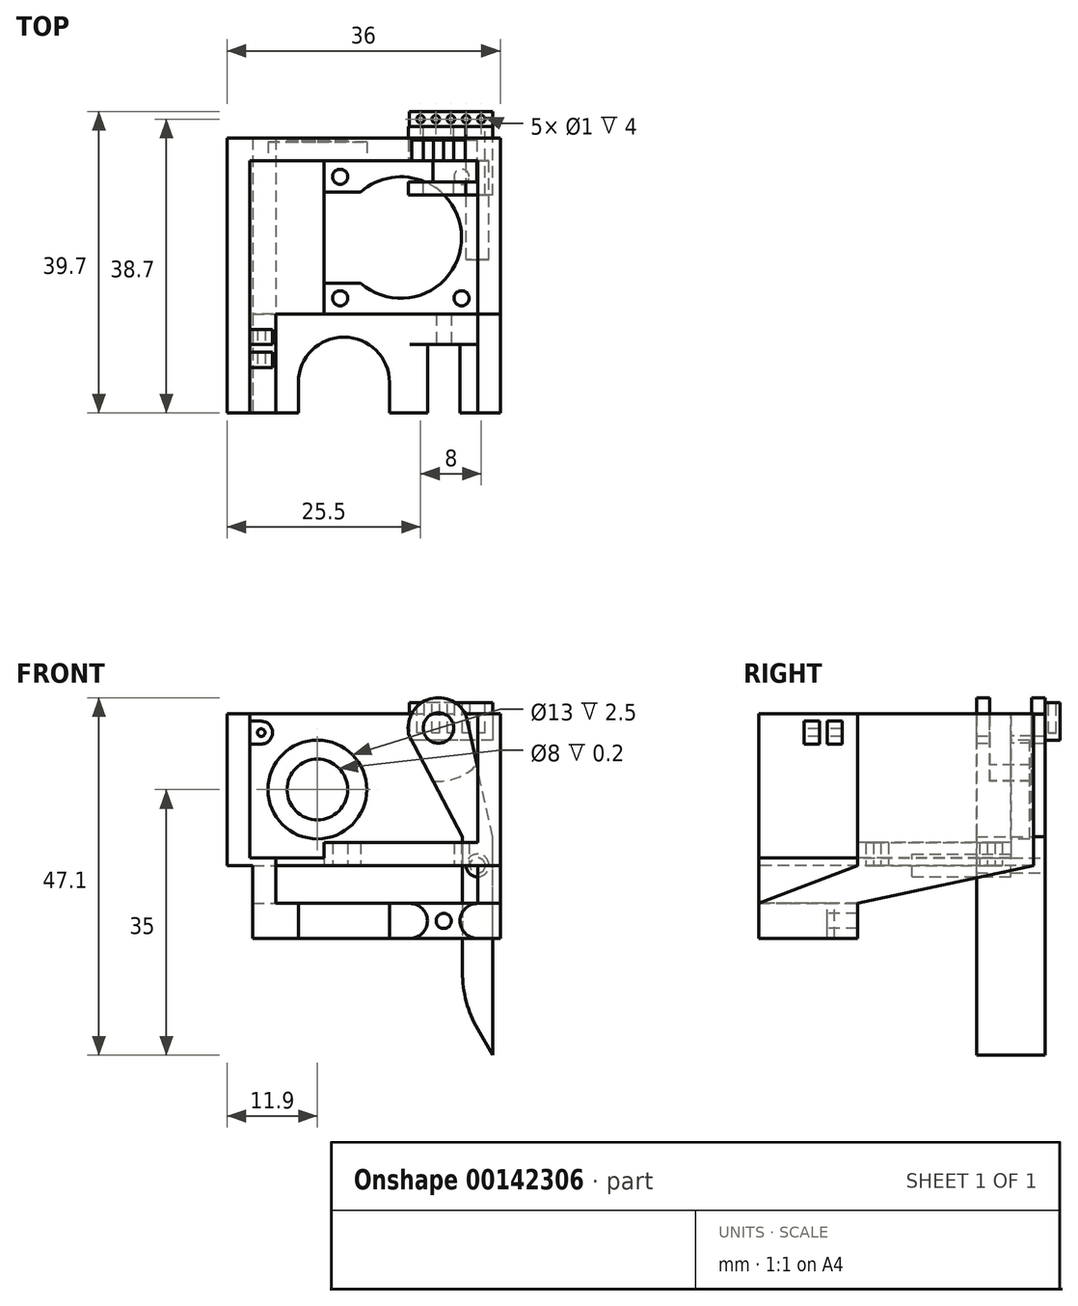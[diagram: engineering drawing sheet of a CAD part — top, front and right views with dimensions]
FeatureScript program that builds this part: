
annotation { "Feature Type Name" : "Feature", "Feature Type Description" : "" }
export const myFeature = defineFeature(function(context is Context, id is Id, definition is map)
    precondition{}
    {
        {
            var Q0;
            Q0=qCreatedBy(makeId("Top.planeOp"),FACE);
            var sketch = newSketch(context, id + "F0", { "sketchPlane" : qUnion([Q0])});
            skLineSegment(sketch, "E0", {"start": v(0, 0) * mm, "end": v(0, -20.2) * mm});
            skLineSegment(sketch, "E1", {"start": v(0, -20.2) * mm, "end": v(3, -20.2) * mm});
            skLineSegment(sketch, "E2", {"start": v(3, -20.2) * mm, "end": v(3, 3) * mm});
            skLineSegment(sketch, "E3", {"start": v(3, 3) * mm, "end": v(-30, 3) * mm});
            skLineSegment(sketch, "E4", {"start": v(-30, 3) * mm, "end": v(-30, 0) * mm});
            skLineSegment(sketch, "E5", {"start": v(-30, 0) * mm, "end": v(0, 0) * mm});
            skLineSegment(sketch, "E6", {"start": v(-4, -20.2) * mm, "end": v(0, -20.2) * mm});
            skCircle(sketch, "E7", {"center": v(-2.1, -2.1) * mm, "radius": 1 * mm});
            skLineSegment(sketch, "E8", {"start": v(3, -20.2) * mm, "end": v(3, -33.2) * mm});
            skLineSegment(sketch, "E9", {"start": v(3, -33.2) * mm, "end": v(-26.6, -33.2) * mm});
            skLineSegment(sketch, "E10", {"start": v(-26.6, -33.2) * mm, "end": v(-26.6, -20.2) * mm});
            skLineSegment(sketch, "E11", {"start": v(-26.6, -20.2) * mm, "end": v(0, -20.2) * mm});
            skArc(sketch, "E12", {"start": v(-11.6, -29.2) * mm, "mid": v(-17.6, -23.2) * mm, "end": v(-23.6, -29.2) * mm});
            skLineSegment(sketch, "E13", {"start": v(-23.6, -33.2) * mm, "end": v(-23.6, -29.2) * mm});
            skLineSegment(sketch, "E14", {"start": v(-11.6, -29.2) * mm, "end": v(-11.6, -33.2) * mm});
            skLineSegment(sketch, "E15", {"start": v(-20.2, 0) * mm, "end": v(-20.2, -20.2) * mm});
            skLineSegment(sketch, "E16", {"start": v(-20.2, -10.1) * mm, "end": v(0, -10.1) * mm, "construction": true});
            skLineSegment(sketch, "E17", {"start": v(-10.1, -20.2) * mm, "end": v(-10.1, 0) * mm, "construction": true});
            skCircle(sketch, "E18", {"center": v(-10.1, -10.1) * mm, "radius": 8 * mm});
            skCircle(sketch, "E19.1.0", {"center": v(-18.1, -2.1) * mm, "radius": 1 * mm});
            skCircle(sketch, "E19.2.0", {"center": v(-18.1, -18.1) * mm, "radius": 1 * mm});
            skCircle(sketch, "E19.3.0", {"center": v(-2.1, -18.1) * mm, "radius": 1 * mm});
            skLineSegment(sketch, "E20", {"start": v(-20.2, -4.1) * mm, "end": v(-15.4, -4.1) * mm});
            skLineSegment(sketch, "E21", {"start": v(-20.2, -16.1) * mm, "end": v(-15.4, -16.1) * mm});
            skLineSegment(sketch, "E22", {"start": v(-30, 3) * mm, "end": v(-33, 3) * mm});
            skLineSegment(sketch, "E23", {"start": v(-33, 3) * mm, "end": v(-33, -33.2) * mm});
            skLineSegment(sketch, "E24", {"start": v(-33, -33.2) * mm, "end": v(-30, -33.2) * mm});
            skLineSegment(sketch, "E25", {"start": v(-30, -33.2) * mm, "end": v(-30, 0) * mm});
            skLineSegment(sketch, "E26", {"start": v(-30, -33.2) * mm, "end": v(-26.6, -33.2) * mm});
            skSolve(sketch);
        }
        {
            var Q0;
            {var subQ0=sQuery(id+"F0.wireOp",EDGE,"E1");Q0=makeQuery(id+"F0.imprint","IMPRINT",FACE,{"disambiguationData":[TD([[makeQuery(id+"F0.imprint","IMPRINT",EDGE,{"derivedFrom":subQ0}),1.0]])]});}
            var Q1;
            Q1=makeQuery(id+"F0.imprint","IMPRINT",FACE,{"disambiguationData":[TD([[makeQuery(id+"F0.imprint","IMPRINT",EDGE,{"derivedFrom":sQuery(id+"F0.wireOp",EDGE,"E4")}),-1.0]])]});
            extrude(context, id + "F1", {"entities" : qUnion([Q0, Q1]), "depth" : 20 * mm});
        }
        {
            var Q0;
            {var subQ1=sQuery(id+"F0.wireOp",EDGE,"E0");Q0=makeQuery(id+"F0.imprint","IMPRINT",FACE,{"disambiguationData":[TD([[makeQuery(id+"F0.imprint","IMPRINT",EDGE,{"derivedFrom":subQ1}),-1.0]])]});}
            extrude(context, id + "F2", {"entities" : qUnion([Q0]), "operationType" : NewBodyOperationType.ADD, "depth" : 3 * mm});
        }
        {
            var Q0;
            Q0=makeQuery(id+"F1.opExtrude","SWEPT_FACE",FACE,{"disambiguationData":[OSD([sQuery(id+"F0.wireOp",EDGE,"E5")])]});
            var sketch = newSketch(context, id + "F3", { "sketchPlane" : qUnion([Q0])});
            skCircle(sketch, "E27", {"center": v(-21.1, 10) * mm, "radius": 6.5 * mm});
            skCircle(sketch, "E28", {"center": v(-21.1, 10) * mm, "radius": 4 * mm});
            skSolve(sketch);
        }
        {
            var Q0;
            Q0=makeQuery(id+"F3.imprint","IMPRINT",FACE,{"disambiguationData":[TD([[makeQuery(id+"F3.imprint","IMPRINT",EDGE,{"derivedFrom":sQuery(id+"F3.wireOp",EDGE,"E28")}),-1.0]])]});
            extrude(context, id + "F4", {"entities" : qUnion([Q0]), "operationType" : NewBodyOperationType.REMOVE, "oppositeDirection" : true, "depth" : 2.5 * mm});
        }
        {
            var Q0;
            Q0=makeQuery(id+"F3.imprint","IMPRINT",FACE,{"disambiguationData":[TD([[makeQuery(id+"F3.imprint","IMPRINT",EDGE,{"derivedFrom":sQuery(id+"F3.wireOp",EDGE,"E28")}),1.0]])]});
            extrude(context, id + "F5", {"entities" : qUnion([Q0]), "operationType" : NewBodyOperationType.REMOVE, "oppositeDirection" : true, "depth" : 2.7 * mm});
        }
        {
            var Q0;
            {var subQ1=sQuery(id+"F0.wireOp",EDGE,"E10");Q0=makeQuery(id+"F0.imprint","IMPRINT",FACE,{"disambiguationData":[TD([[makeQuery(id+"F0.imprint","IMPRINT",EDGE,{"derivedFrom":subQ1}),1.0]])]});}
            extrude(context, id + "F6", {"entities" : qUnion([Q0]), "operationType" : NewBodyOperationType.ADD, "depth" : 1 * mm});
        }
        {
            var Q0;
            Q0=qCreatedBy(makeId("Top.planeOp"),FACE);
            cPlane(context, id + "F7", {"entities" : qUnion([Q0]), "cplaneType" : CPlaneType.OFFSET, "offset" : 5 * mm, "oppositeDirection" : true, "width" : 150 * mm, "height" : 150 * mm});
        }
        {
            var Q0;
            Q0=qCreatedBy(id+"F7.planeOp",FACE);
            var sketch = newSketch(context, id + "F8", { "sketchPlane" : qUnion([Q0])});
            skLineSegment(sketch, "E29.0.0", {"start": v(3, -20.2) * mm, "end": v(0, -20.2) * mm});
            skLineSegment(sketch, "E29.0.1", {"start": v(0, -20.2) * mm, "end": v(-4, -20.2) * mm});
            skLineSegment(sketch, "E29.0.2", {"start": v(-4, -20.2) * mm, "end": v(-20.2, -20.2) * mm});
            skLineSegment(sketch, "E29.0.3", {"start": v(-20.2, -20.2) * mm, "end": v(-26.6, -20.2) * mm});
            skLineSegment(sketch, "E29.0.4", {"start": v(-26.6, -20.2) * mm, "end": v(-26.6, -33.2) * mm});
            skLineSegment(sketch, "E29.0.5", {"start": v(-26.6, -33.2) * mm, "end": v(-23.6, -33.2) * mm});
            skLineSegment(sketch, "E29.0.6", {"start": v(-23.6, -33.2) * mm, "end": v(-23.6, -29.2) * mm});
            skArc(sketch, "E29.0.7", {"start": v(-23.6, -29.2) * mm, "mid": v(-17.6, -23.2) * mm, "end": v(-11.6, -29.2) * mm});
            skLineSegment(sketch, "E29.0.8", {"start": v(-11.6, -29.2) * mm, "end": v(-11.6, -33.2) * mm});
            skLineSegment(sketch, "E29.0.9", {"start": v(-11.6, -33.2) * mm, "end": v(3, -33.2) * mm});
            skLineSegment(sketch, "E29.0.10", {"start": v(3, -33.2) * mm, "end": v(3, -20.2) * mm});
            skSolve(sketch);
        }
        {
            var Q0;
            Q0 = qSketchRegion(id + "F8", true);
            extrude(context, id + "F9", {"entities" : qUnion([Q0]), "oppositeDirection" : true, "depth" : 4.6 * mm});
        }
        {
            var Q0;
            Q0=makeQuery(id+"F1.opExtrude","SWEPT_FACE",FACE,{"disambiguationData":[OSD([sQuery(id+"F0.wireOp",EDGE,"E2")])]});
            var sketch = newSketch(context, id + "F10", { "sketchPlane" : qUnion([Q0])});
            skPoint(sketch, "E30.0", {"position": v(-33.2, -5) * mm});
            skPoint(sketch, "E31.0", {"position": v(-20.2, -5) * mm});
            skPoint(sketch, "E32.0", {"position": v(-20.2, 0) * mm});
            skLineSegment(sketch, "E33.0", {"start": v(-20.2, 0) * mm, "end": v(3, 0) * mm});
            skLineSegment(sketch, "E34", {"start": v(-33.2, -5) * mm, "end": v(-20.2, 0) * mm});
            skLineSegment(sketch, "E35", {"start": v(-20.2, -5) * mm, "end": v(3, 0) * mm});
            skLineSegment(sketch, "E36", {"start": v(-33.2, -5) * mm, "end": v(-20.2, -5) * mm});
            skSolve(sketch);
        }
        {
            var Q0;
            Q0 = qSketchRegion(id + "F10", true);
            extrude(context, id + "F11", {"entities" : qUnion([Q0]), "operationType" : NewBodyOperationType.ADD, "oppositeDirection" : true, "depth" : 3 * mm});
        }
        {
            var Q0;
            Q0=makeQuery(id+"F9.opExtrude","SWEPT_FACE",FACE,{"disambiguationData":[OSD([sQuery(id+"F8.wireOp",EDGE,"E29.0.4")])]});
            var sketch = newSketch(context, id + "F12", { "sketchPlane" : qUnion([Q0])});
            skLineSegment(sketch, "E37.0", {"start": v(-3, 0) * mm, "end": v(33.2, 0) * mm});
            skLineSegment(sketch, "E38", {"start": v(-3, 0) * mm, "end": v(20.2, -5) * mm});
            skLineSegment(sketch, "E39", {"start": v(33.2, 0) * mm, "end": v(33.2, -5) * mm});
            skLineSegment(sketch, "E40", {"start": v(20.2, -5) * mm, "end": v(20.2, -9.6) * mm});
            skLineSegment(sketch, "E41", {"start": v(20.2, -9.6) * mm, "end": v(33.2, -9.6) * mm});
            skLineSegment(sketch, "E42", {"start": v(33.2, -9.6) * mm, "end": v(33.2, -5) * mm});
            skSolve(sketch);
        }
        {
            var Q0;
            Q0 = qSketchRegion(id + "F12", true);
            extrude(context, id + "F13", {"entities" : qUnion([Q0]), "operationType" : NewBodyOperationType.ADD, "depth" : 3 * mm});
        }
        {
            var Q0;
            Q0=qCreatedBy(makeId("Front.planeOp"),FACE);
            var sketch = newSketch(context, id + "F14", { "sketchPlane" : qUnion([Q0])});
            skCircle(sketch, "E43", {"center": v(0, 0) * mm, "radius": 1 * mm});
            skArc(sketch, "E44", {"start": v(-1.58, 19.92) * mm, "mid": v(-6.6, 21.83) * mm, "end": v(-9, 17.03) * mm});
            skLineSegment(sketch, "E45", {"start": v(-9, 17.03) * mm, "end": v(-2, 3.8) * mm});
            skLineSegment(sketch, "E46", {"start": v(-2, 3.8) * mm, "end": v(-2, -14.05) * mm});
            skLineSegment(sketch, "E47", {"start": v(0, -21.55) * mm, "end": v(2, -25) * mm});
            skLineSegment(sketch, "E48", {"start": v(2, -25) * mm, "end": v(2, 3.8) * mm});
            skLineSegment(sketch, "E49", {"start": v(2, 3.8) * mm, "end": v(-1.58, 19.92) * mm});
            skPoint(sketch, "E50.visualSharp", {"position": v(-2, -18.07) * mm});
            skArc(sketch, "E50.filletArc", {"start": v(-2, -14.05) * mm, "mid": v(-1.49, -17.93) * mm, "end": v(0, -21.55) * mm});
            skCircle(sketch, "E51", {"center": v(-5.15, 18.1) * mm, "radius": 7 * mm});
            skCircle(sketch, "E52", {"center": v(-5.15, 18.1) * mm, "radius": 2 * mm});
            skSolve(sketch);
        }
        {
            var Q0;
            Q0=makeQuery(id+"F14.imprint","IMPRINT",FACE,{"disambiguationData":[TD([[makeQuery(id+"F14.imprint","IMPRINT",EDGE,{"derivedFrom":sQuery(id+"F14.wireOp",EDGE,"3w4kYvQP-Kg79-7WvC-1bv6-1XLRH75UkTbv")}),-1.0]])]});
            var Q1;
            Q1=makeQuery(id+"F14.imprint","IMPRINT",FACE,{"disambiguationData":[TD([[makeQuery(id+"F14.imprint","IMPRINT",EDGE,{"derivedFrom":sQuery(id+"F14.wireOp",EDGE,"E43")}),-1.0]])]});
            var Q2;
            Q2=makeQuery(id+"F14.imprint","IMPRINT",FACE,{"disambiguationData":[TD([[makeQuery(id+"F14.imprint","IMPRINT",EDGE,{"derivedFrom":sQuery(id+"F14.wireOp",EDGE,"E52")}),-1.0]])]});
            var Q3;
            {var subQ0=sQuery(id+"F14.wireOp",EDGE,"RrWphAZK-CFIM-2zWL-3FTu-twPML3PgQJvA");Q3=makeQuery(id+"F14.imprint","IMPRINT",FACE,{"disambiguationData":[TD([[makeQuery(id+"F14.imprint","IMPRINT",EDGE,{"derivedFrom":subQ0}),1.0]])]});}
            var Q4;
            {var subQ0=sQuery(id+"F14.wireOp",EDGE,"azYlIIop-X9Vr-JewF-sj9w-C3T44Yyx2HpW");Q4=makeQuery(id+"F14.imprint","IMPRINT",FACE,{"disambiguationData":[TD([[makeQuery(id+"F14.imprint","IMPRINT",EDGE,{"derivedFrom":subQ0}),-1.0]])]});}
            var Q5;
            {var subQ0=sQuery(id+"F14.wireOp",EDGE,"GTiJ9Pga-DqQH-IdMt-MPS1-rSJpsFrb6ygz");Q5=makeQuery(id+"F14.imprint","IMPRINT",FACE,{"disambiguationData":[TD([[makeQuery(id+"F14.imprint","IMPRINT",EDGE,{"derivedFrom":subQ0}),1.0]])]});}
            extrude(context, id + "F15", {"entities" : qUnion([Q0, Q1, Q2, Q3, Q4, Q5]), "endBound" : BoundingType.SYMMETRIC, "depth" : 9 * mm});
        }
        {
            var Q0;
            Q0=makeQuery(id+"F14.imprint","IMPRINT",FACE,{"disambiguationData":[TD([[makeQuery(id+"F14.imprint","IMPRINT",EDGE,{"derivedFrom":sQuery(id+"F14.wireOp",EDGE,"3w4kYvQP-Kg79-7WvC-1bv6-1XLRH75UkTbv")}),-1.0]])]});
            var Q1;
            {var subQ0=sQuery(id+"F14.wireOp",EDGE,"RrWphAZK-CFIM-2zWL-3FTu-twPML3PgQJvA");Q1=makeQuery(id+"F14.imprint","IMPRINT",FACE,{"disambiguationData":[TD([[makeQuery(id+"F14.imprint","IMPRINT",EDGE,{"derivedFrom":subQ0}),1.0]])]});}
            var Q2;
            {var subQ3=sQuery(id+"F14.wireOp",EDGE,"RrWphAZK-CFIM-2zWL-3FTu-twPML3PgQJvA");Q2=makeQuery(id+"F14.imprint","IMPRINT",FACE,{"disambiguationData":[TD([[makeQuery(id+"F14.imprint","IMPRINT",EDGE,{"derivedFrom":subQ3}),-1.0]])]});}
            var Q3;
            Q3=makeQuery(id+"F14.imprint","IMPRINT",FACE,{"disambiguationData":[TD([[makeQuery(id+"F14.imprint","IMPRINT",EDGE,{"derivedFrom":sQuery(id+"F14.wireOp",EDGE,"E52")}),-1.0]])]});
            var Q4;
            {var subQ0=sQuery(id+"F14.wireOp",EDGE,"GTiJ9Pga-DqQH-IdMt-MPS1-rSJpsFrb6ygz");Q4=makeQuery(id+"F14.imprint","IMPRINT",FACE,{"disambiguationData":[TD([[makeQuery(id+"F14.imprint","IMPRINT",EDGE,{"derivedFrom":subQ0}),1.0]])]});}
            extrude(context, id + "F16", {"entities" : qUnion([Q0, Q1, Q2, Q3, Q4]), "operationType" : NewBodyOperationType.REMOVE, "endBound" : BoundingType.SYMMETRIC, "oppositeDirection" : true, "depth" : 5.5 * mm});
        }
        {
            var Q0;
            Q0=qCreatedBy(makeId("Front.planeOp"),FACE);
            var sketch = newSketch(context, id + "F17", { "sketchPlane" : qUnion([Q0])});
            skCircle(sketch, "E53", {"center": v(0, 0) * mm, "radius": 1.5 * mm});
            skSolve(sketch);
        }
        {
            var Q0;
            Q0 = qSketchRegion(id + "F17", true);
            extrude(context, id + "F18", {"entities" : qUnion([Q0]), "depth" : 13 * mm});
        }
        {
            var Q0;
            Q0=makeQuery(id+"F1.opExtrude","SWEPT_FACE",FACE,{"disambiguationData":[OSD([sQuery(id+"F0.wireOp",EDGE,"E25")])]});
            var sketch = newSketch(context, id + "F19", { "sketchPlane" : qUnion([Q0])});
            skLineSegment(sketch, "E54.bottom", {"start": v(-27.2, 19) * mm, "end": v(-25.2, 19) * mm});
            skLineSegment(sketch, "E54.top", {"start": v(-27.2, 16) * mm, "end": v(-25.2, 16) * mm});
            skLineSegment(sketch, "E54.left", {"start": v(-27.2, 19) * mm, "end": v(-27.2, 16) * mm});
            skLineSegment(sketch, "E54.right", {"start": v(-25.2, 19) * mm, "end": v(-25.2, 16) * mm});
            skLineSegment(sketch, "E55.bottom", {"start": v(-24.2, 19) * mm, "end": v(-22.2, 19) * mm});
            skLineSegment(sketch, "E55.top", {"start": v(-24.2, 16) * mm, "end": v(-22.2, 16) * mm});
            skLineSegment(sketch, "E55.left", {"start": v(-24.2, 19) * mm, "end": v(-24.2, 16) * mm});
            skLineSegment(sketch, "E55.right", {"start": v(-22.2, 19) * mm, "end": v(-22.2, 16) * mm});
            skSolve(sketch);
        }
        {
            var Q0;
            Q0 = qSketchRegion(id + "F19", true);
            extrude(context, id + "F20", {"entities" : qUnion([Q0]), "operationType" : NewBodyOperationType.ADD, "depth" : 3 * mm});
        }
        {
            var Q0;
            Q0=makeQuery(id+"F20.opExtrude","SWEPT_FACE",FACE,{"disambiguationData":[OSD([sQuery(id+"F19.wireOp",EDGE,"E54.left")])]});
            var sketch = newSketch(context, id + "F21", { "sketchPlane" : qUnion([Q0])});
            skCircle(sketch, "E56", {"center": v(-28.5, 17.5) * mm, "radius": 0.5 * mm});
            skArc(sketch, "E57", {"start": v(-28.5, 16) * mm, "mid": v(-27, 17.5) * mm, "end": v(-28.5, 19) * mm});
            skLineSegment(sketch, "E58.0", {"start": v(-28.5, 19) * mm, "end": v(-30, 19) * mm});
            skLineSegment(sketch, "E59.0", {"start": v(-28.5, 16) * mm, "end": v(-30, 16) * mm});
            skPoint(sketch, "E60.orphan", {"position": v(-27, 19) * mm});
            skPoint(sketch, "E61.orphan", {"position": v(-27, 16) * mm});
            skSolve(sketch);
        }
        {
            var Q0;
            Q0 = qSketchRegion(id + "F21", true);
            var Q1;
            {var subQ0=sQuery(id+"F21.wireOp",EDGE,"E57");var subQ1=sQuery(id+"F19.wireOp",EDGE,"E54.left");var subQ4=makeQuery(id+"F20.opExtrude","CAP_EDGE",EDGE,{"disambiguationData":[OSD([subQ1])],"isStart":false});var subQ5=makeQuery(id+"F21.imprint","INTERSECT",VERTEX,{"derivedFrom":[subQ4,subQ0]});Q1=makeQuery(id+"F21.imprint","IMPRINT",FACE,{"disambiguationData":[TD([[makeQuery(id+"F21.imprint","IMPRINT",EDGE,{"disambiguationData":[TD([[subQ5,1.0]])],"derivedFrom":subQ4}),-1.0]])]});}
            var Q2;
            {var subQ0=sQuery(id+"F21.wireOp",EDGE,"E57");var subQ1=sQuery(id+"F19.wireOp",EDGE,"E54.left");var subQ4=makeQuery(id+"F20.opExtrude","CAP_EDGE",EDGE,{"disambiguationData":[OSD([subQ1])],"isStart":false});var subQ5=makeQuery(id+"F21.imprint","INTERSECT",VERTEX,{"derivedFrom":[subQ4,subQ0]});Q2=makeQuery(id+"F21.imprint","IMPRINT",FACE,{"disambiguationData":[TD([[makeQuery(id+"F21.imprint","IMPRINT",EDGE,{"disambiguationData":[TD([[subQ5,-1.0]])],"derivedFrom":subQ4}),-1.0]])]});}
            var Q3;
            Q3=makeQuery(id+"F20.opExtrude","SWEPT_FACE",FACE,{"disambiguationData":[OSD([sQuery(id+"F19.wireOp",EDGE,"E55.right")])]});
            extrude(context, id + "F22", {"entities" : qUnion([Q0, Q1, Q2]), "operationType" : NewBodyOperationType.REMOVE, "endBound" : BoundingType.UP_TO_SURFACE, "oppositeDirection" : true, "endBoundEntityFace" : qUnion([Q3]), "depth" : 25 * mm});
        }
        {
            var Q0;
            Q0=makeQuery(id+"F15.opExtrude","CAP_FACE",FACE,{"disambiguationData":[OSD([sQuery(id+"F14.wireOp",EDGE,"E43"),sQuery(id+"F14.wireOp",EDGE,"E44"),sQuery(id+"F14.wireOp",EDGE,"E45"),sQuery(id+"F14.wireOp",EDGE,"E46"),sQuery(id+"F14.wireOp",EDGE,"E47"),sQuery(id+"F14.wireOp",EDGE,"E48"),sQuery(id+"F14.wireOp",EDGE,"E49"),sQuery(id+"F14.wireOp",EDGE,"E50.filletArc"),sQuery(id+"F14.wireOp",EDGE,"E51"),sQuery(id+"F14.wireOp",EDGE,"azYlIIop-X9Vr-JewF-sj9w-C3T44Yyx2HpW"),sQuery(id+"F14.wireOp",EDGE,"yiFGDsk1-bvDu-piiR-qnhc-R5yeL4BFpwlV"),sQuery(id+"F14.wireOp",EDGE,"2SAPdYRY-FjJB-TBLT-5of9-lJQlkSxIarlX"),sQuery(id+"F14.wireOp",EDGE,"RrWphAZK-CFIM-2zWL-3FTu-twPML3PgQJvA"),sQuery(id+"F14.wireOp",EDGE,"E52")])],"isStart":true});
            var sketch = newSketch(context, id + "F23", { "sketchPlane" : qUnion([Q0])});
            skLineSegment(sketch, "E62.bottom", {"start": v(-2, 21.44) * mm, "end": v(9, 21.44) * mm});
            skLineSegment(sketch, "E62.top", {"start": v(-2, 16.49) * mm, "end": v(9, 16.49) * mm});
            skLineSegment(sketch, "E62.left", {"start": v(-2, 21.44) * mm, "end": v(-2, 16.49) * mm});
            skLineSegment(sketch, "E62.right", {"start": v(9, 21.44) * mm, "end": v(9, 16.49) * mm});
            skLineSegment(sketch, "E63.0", {"start": v(-2, -25) * mm, "end": v(-2, 3.8) * mm});
            skSolve(sketch);
        }
        {
            var Q0;
            Q0 = qSketchRegion(id + "F23", true);
            extrude(context, id + "F24", {"entities" : qUnion([Q0]), "operationType" : NewBodyOperationType.ADD, "depth" : 2 * mm});
        }
        {
            var Q0;
            Q0=makeQuery(id+"F24.boolean.opBoolean","MERGE",FACE,{"derivedFrom":[makeQuery(id+"F15.opExtrude","SWEPT_FACE",FACE,{"disambiguationData":[OSD([sQuery(id+"F14.wireOp",EDGE,"azYlIIop-X9Vr-JewF-sj9w-C3T44Yyx2HpW"),sQuery(id+"F14.wireOp",EDGE,"RrWphAZK-CFIM-2zWL-3FTu-twPML3PgQJvA")])]}),makeQuery(id+"F24.opExtrude","SWEPT_FACE",FACE,{"disambiguationData":[OSD([sQuery(id+"F23.wireOp",EDGE,"E62.bottom")])]})]});
            var sketch = newSketch(context, id + "F25", { "sketchPlane" : qUnion([Q0])});
            skCircle(sketch, "E64", {"center": v(0.5, 5.5) * mm, "radius": 0.5 * mm});
            skLineSegment(sketch, "E65", {"start": v(-9, 4.5) * mm, "end": v(2, 4.5) * mm, "construction": true});
            skCircle(sketch, "E66.1.0.0", {"center": v(-1.5, 5.5) * mm, "radius": 0.5 * mm});
            skCircle(sketch, "E66.2.0.0", {"center": v(-3.5, 5.5) * mm, "radius": 0.5 * mm});
            skLineSegment(sketch, "E66.direction1", {"start": v(0.5, 5.5) * mm, "end": v(-1.5, 5.5) * mm, "construction": true});
            skCircle(sketch, "E67.0.3.0", {"center": v(-5.5, 5.5) * mm, "radius": 0.5 * mm});
            skCircle(sketch, "E67.0.4.0", {"center": v(-7.5, 5.5) * mm, "radius": 0.5 * mm});
            skSolve(sketch);
        }
        {
            var Q0;
            Q0 = qSketchRegion(id + "F25", true);
            extrude(context, id + "F26", {"entities" : qUnion([Q0]), "operationType" : NewBodyOperationType.REMOVE, "oppositeDirection" : true, "depth" : 4 * mm});
        }
        {
            var Q0;
            Q0=makeQuery(id+"F9.opExtrude","SWEPT_FACE",FACE,{"disambiguationData":[OSD([sQuery(id+"F8.wireOp",EDGE,"E29.0.9")])]});
            var sketch = newSketch(context, id + "F27", { "sketchPlane" : qUnion([Q0])});
            skLineSegment(sketch, "E68.0", {"start": v(-11.6, -5) * mm, "end": v(0, -5) * mm});
            skLineSegment(sketch, "E69.0", {"start": v(-11.6, -9.6) * mm, "end": v(3, -9.6) * mm});
            skArc(sketch, "E70", {"start": v(-8.9, -9.6) * mm, "mid": v(-6.6, -7.3) * mm, "end": v(-8.9, -5) * mm});
            skArc(sketch, "E71", {"start": v(0, -5) * mm, "mid": v(-2.3, -7.3) * mm, "end": v(0, -9.6) * mm});
            skCircle(sketch, "E72", {"center": v(-4.45, -7.3) * mm, "radius": 1 * mm});
            skSolve(sketch);
        }
        {
            var Q0;
            {var subQ1=sQuery(id+"F27.wireOp",EDGE,"E70");Q0=makeQuery(id+"F27.imprint","IMPRINT",FACE,{"disambiguationData":[TD([[makeQuery(id+"F27.imprint","IMPRINT",EDGE,{"derivedFrom":subQ1}),-1.0]])]});}
            var Q1;
            Q1=makeQuery(id+"F27.imprint","IMPRINT",FACE,{"disambiguationData":[TD([[makeQuery(id+"F27.imprint","IMPRINT",EDGE,{"derivedFrom":sQuery(id+"F27.wireOp",EDGE,"E72")}),1.0]])]});
            extrude(context, id + "F28", {"entities" : qUnion([Q0, Q1]), "operationType" : NewBodyOperationType.REMOVE, "oppositeDirection" : true, "depth" : 9 * mm});
        }
        {
            var Q0;
            Q0=makeQuery(id+"F27.imprint","IMPRINT",FACE,{"disambiguationData":[TD([[makeQuery(id+"F27.imprint","IMPRINT",EDGE,{"derivedFrom":sQuery(id+"F27.wireOp",EDGE,"E72")}),1.0]])]});
            extrude(context, id + "F29", {"entities" : qUnion([Q0]), "operationType" : NewBodyOperationType.REMOVE, "endBound" : BoundingType.THROUGH_ALL, "oppositeDirection" : true, "depth" : 12 * mm});
        }
    });
